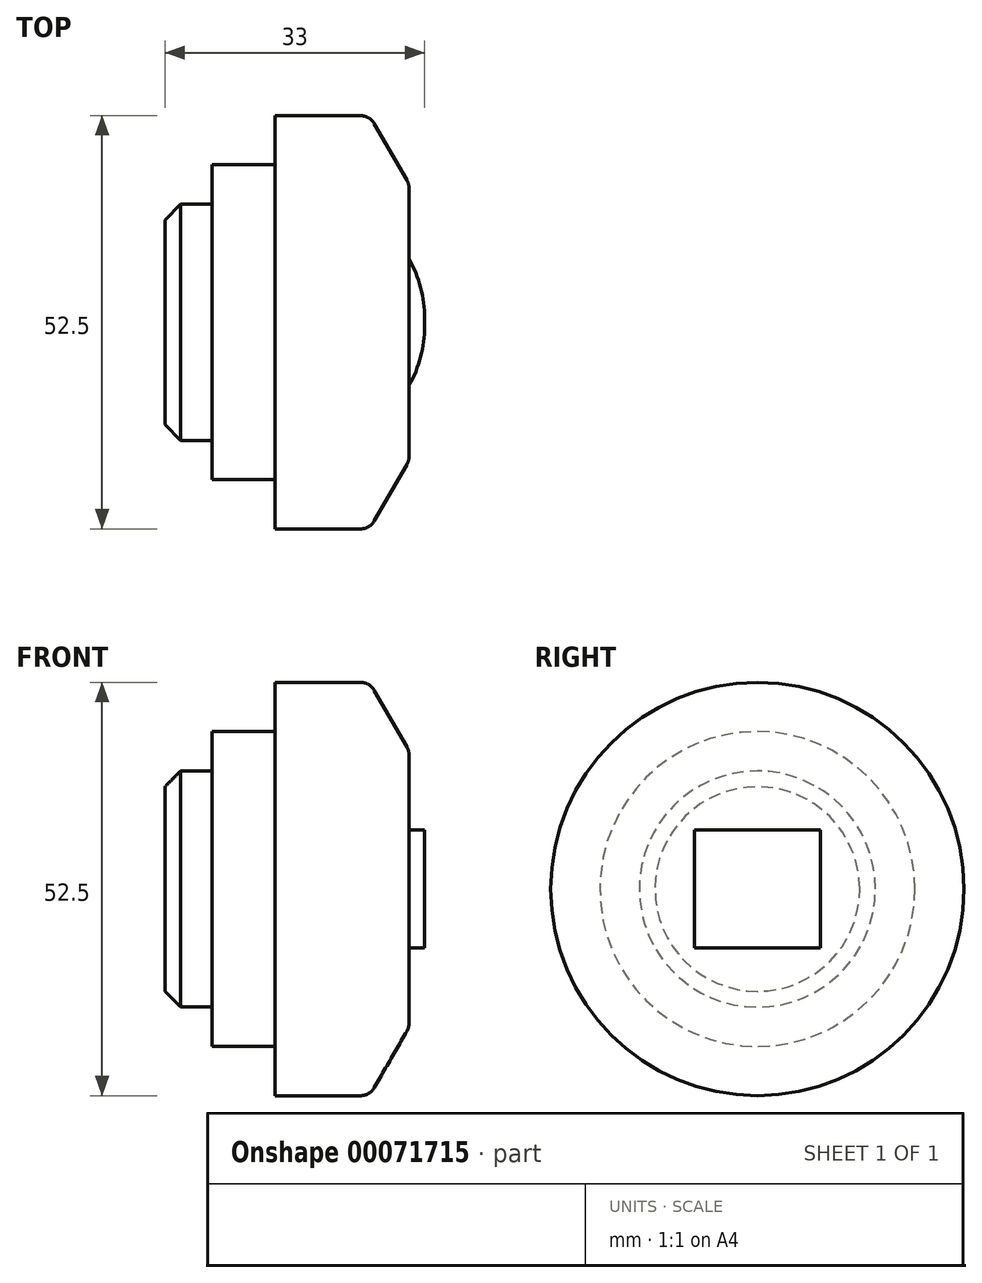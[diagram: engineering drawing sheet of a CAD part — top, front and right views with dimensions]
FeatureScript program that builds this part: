
annotation { "Feature Type Name" : "Feature", "Feature Type Description" : "" }
export const myFeature = defineFeature(function(context is Context, id is Id, definition is map)
    precondition{}
    {
        {
            var Q0;
            Q0=qCreatedBy(makeId("Front.planeOp"),FACE);
            var sketch = newSketch(context, id + "F0", { "sketchPlane" : qUnion([Q0])});
            skLineSegment(sketch, "E0", {"start": v(0, 0) * mm, "end": v(0, 15) * mm});
            skLineSegment(sketch, "E1", {"start": v(0, 15) * mm, "end": v(6, 15) * mm});
            skLineSegment(sketch, "E2", {"start": v(6, 15) * mm, "end": v(6, 20) * mm});
            skLineSegment(sketch, "E3", {"start": v(6, 20) * mm, "end": v(14, 20) * mm});
            skLineSegment(sketch, "E4", {"start": v(14, 20) * mm, "end": v(14, 26.25) * mm});
            skLineSegment(sketch, "E5", {"start": v(14, 26.25) * mm, "end": v(31, 26.25) * mm});
            skLineSegment(sketch, "E6", {"start": v(31, 26.25) * mm, "end": v(31, 0) * mm});
            skLineSegment(sketch, "E7", {"start": v(0, 0) * mm, "end": v(31, 0) * mm});
            skSolve(sketch);
        }
        {
            var Q0;
            Q0=qCreatedBy(makeId("Front.planeOp"),FACE);
            var sketch = newSketch(context, id + "F1", { "sketchPlane" : qUnion([Q0])});
            skLineSegment(sketch, "E8", {"start": v(0, 0) * mm, "end": v(87.42, 0) * mm});
            skSolve(sketch);
        }
        {
            var Q0;
            Q0=makeQuery(id+"F0.imprint","IMPRINT",FACE,{"disambiguationData":[TD([[makeQuery(id+"F0.imprint","IMPRINT",EDGE,{"derivedFrom":sQuery(id+"F0.wireOp",EDGE,"E0")}),-1.0]])]});
            var Q1;
            Q1=sQuery(id+"F1.wireOp",EDGE,"E8");
            revolve(context, id + "F2", {"entities" : qUnion([Q0]), "axis" : qUnion([Q1]), "revolveType" : RevolveType.FULL});
        }
        {
            var Q0;
            Q0=makeQuery(id+"F2.opRevolve","SWEPT_EDGE",EDGE,{"disambiguationData":[OSD([sQuery(id+"F0.wireOp",EDGE,"E0"),sQuery(id+"F0.wireOp",EDGE,"E1")])]});
            chamfer(context, id + "F3", {"entities" : qUnion([Q0]), "width" : 2 * mm, "tangentPropagation" : true});
        }
        {
            var Q0;
            Q0=makeQuery(id+"F2.opRevolve","SWEPT_EDGE",EDGE,{"disambiguationData":[OSD([sQuery(id+"F0.wireOp",EDGE,"E5"),sQuery(id+"F0.wireOp",EDGE,"E6")])]});
            chamfer(context, id + "F4", {"entities" : qUnion([Q0]), "chamferType" : ChamferType.OFFSET_ANGLE, "width" : 5 * mm, "oppositeDirection" : false, "angle" : 60 * degree, "tangentPropagation" : true});
        }
        {
            var Q0;
            {var subQ0=sQuery(id+"F0.wireOp",EDGE,"E5");Q0=makeQuery(id+"F4.opChamfer","BLEND_EDGE",EDGE,{"blendedFrom":[makeQuery(id+"F2.opRevolve","SWEPT_EDGE",EDGE,{"disambiguationData":[OSD([subQ0,sQuery(id+"F0.wireOp",EDGE,"E6")])]}),makeQuery(id+"F2.opRevolve","SWEPT_FACE",FACE,{"disambiguationData":[OSD([subQ0])]})],"blendedInto":[makeQuery(id+"F2.opRevolve","SWEPT_FACE",FACE,{"disambiguationData":[OSD([subQ0])]})]});}
            var Q1;
            {var subQ0=sQuery(id+"F0.wireOp",EDGE,"E6");Q1=makeQuery(id+"F4.opChamfer","BLEND_EDGE",EDGE,{"blendedFrom":[makeQuery(id+"F2.opRevolve","SWEPT_EDGE",EDGE,{"disambiguationData":[OSD([sQuery(id+"F0.wireOp",EDGE,"E5"),subQ0])]}),makeQuery(id+"F2.opRevolve","SWEPT_FACE",FACE,{"disambiguationData":[OSD([subQ0])]})],"blendedInto":[makeQuery(id+"F2.opRevolve","SWEPT_FACE",FACE,{"disambiguationData":[OSD([subQ0])]})]});}
            fillet(context, id + "F5", {"entities" : qUnion([Q0, Q1]), "radius" : 2 * mm, "tangentPropagation" : true, "allowEdgeOverflow" : false});
        }
        {
            var Q0;
            Q0=makeQuery(id+"F2.opRevolve","SWEPT_FACE",FACE,{"disambiguationData":[OSD([sQuery(id+"F0.wireOp",EDGE,"E6")])]});
            var sketch = newSketch(context, id + "F6", { "sketchPlane" : qUnion([Q0])});
            skLineSegment(sketch, "E9.bottom", {"start": v(-8, 7.5) * mm, "end": v(8, 7.5) * mm});
            skLineSegment(sketch, "E9.top", {"start": v(-8, -7.5) * mm, "end": v(8, -7.5) * mm});
            skLineSegment(sketch, "E9.left", {"start": v(-8, 7.5) * mm, "end": v(-8, -7.5) * mm});
            skLineSegment(sketch, "E9.right", {"start": v(8, 7.5) * mm, "end": v(8, -7.5) * mm});
            skSolve(sketch);
        }
        {
            var Q0;
            Q0=makeQuery(id+"F6.imprint","IMPRINT",FACE,{"disambiguationData":[TD([[makeQuery(id+"F6.imprint","IMPRINT",EDGE,{"derivedFrom":sQuery(id+"F6.wireOp",EDGE,"E9.bottom")}),-1.0]])]});
            extrude(context, id + "F7", {"entities" : qUnion([Q0]), "operationType" : NewBodyOperationType.ADD, "depth" : 2 * mm});
        }
        {
            var Q0;
            Q0=makeQuery(id+"F7.opExtrude","CAP_EDGE",EDGE,{"disambiguationData":[OSD([sQuery(id+"F6.wireOp",EDGE,"E9.left")])],"isStart":false});
            var Q1;
            Q1=makeQuery(id+"F7.opExtrude","CAP_EDGE",EDGE,{"disambiguationData":[OSD([sQuery(id+"F6.wireOp",EDGE,"E9.right")])],"isStart":false});
            fillet(context, id + "F8", {"entities" : qUnion([Q0, Q1]), "radius" : 15 * mm, "tangentPropagation" : true, "allowEdgeOverflow" : false});
        }
    });
